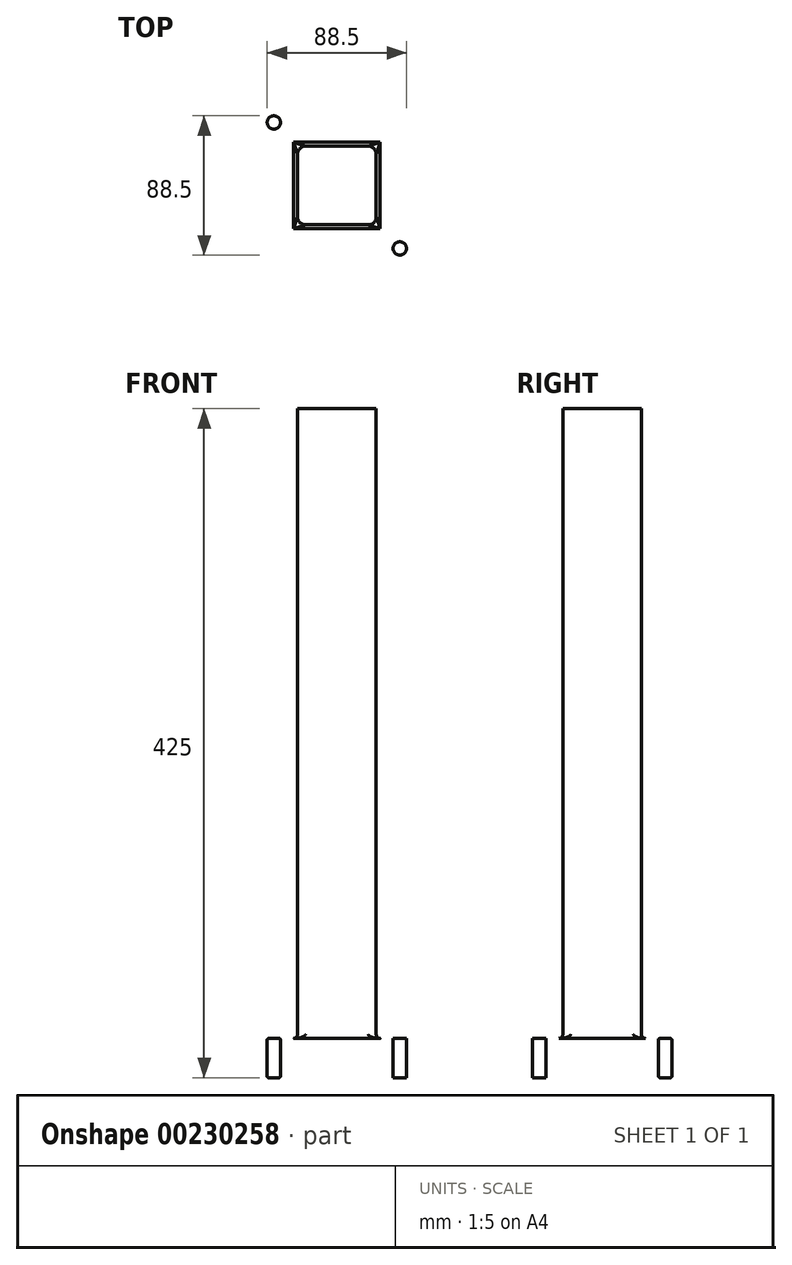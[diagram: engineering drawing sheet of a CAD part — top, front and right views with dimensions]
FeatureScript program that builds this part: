
annotation { "Feature Type Name" : "Feature", "Feature Type Description" : "" }
export const myFeature = defineFeature(function(context is Context, id is Id, definition is map)
    precondition{}
    {
        {
            var Q0;
            Q0=qCreatedBy(makeId("Front.planeOp"),FACE);
            var sketch = newSketch(context, id + "F0", { "sketchPlane" : qUnion([Q0])});
            skLineSegment(sketch, "E0.bottom", {"start": v(25, 200) * mm, "end": v(-25, 200) * mm});
            skLineSegment(sketch, "E0.top", {"start": v(25, -200) * mm, "end": v(-25, -200) * mm});
            skLineSegment(sketch, "E0.left", {"start": v(25, 200) * mm, "end": v(25, -200) * mm});
            skLineSegment(sketch, "E0.right", {"start": v(-25, 200) * mm, "end": v(-25, -200) * mm});
            skPoint(sketch, "E0.middle", {"position": v(0, 0) * mm});
            skLineSegment(sketch, "E1.bottom", {"start": v(-50, -200) * mm, "end": v(50, -200) * mm});
            skLineSegment(sketch, "E1.top", {"start": v(-50, -225) * mm, "end": v(50, -225) * mm});
            skLineSegment(sketch, "E1.left", {"start": v(-50, -200) * mm, "end": v(-50, -225) * mm});
            skLineSegment(sketch, "E1.right", {"start": v(50, -200) * mm, "end": v(50, -225) * mm});
            skSolve(sketch);
        }
        {
            var Q0;
            Q0=makeQuery(id+"F0.imprint","IMPRINT",FACE,{"disambiguationData":[TD([[makeQuery(id+"F0.imprint","IMPRINT",EDGE,{"derivedFrom":sQuery(id+"F0.wireOp",EDGE,"E1.top")}),1.0]])]});
            extrude(context, id + "F1", {"entities" : qUnion([Q0]), "endBound" : BoundingType.SYMMETRIC, "depth" : 100 * mm});
        }
        {
            var Q0;
            Q0=makeQuery(id+"F0.imprint","IMPRINT",FACE,{"disambiguationData":[TD([[makeQuery(id+"F0.imprint","IMPRINT",EDGE,{"derivedFrom":sQuery(id+"F0.wireOp",EDGE,"E0.bottom")}),1.0]])]});
            extrude(context, id + "F2", {"entities" : qUnion([Q0]), "operationType" : NewBodyOperationType.ADD, "endBound" : BoundingType.SYMMETRIC, "depth" : 50 * mm});
        }
        {
            var Q0;
            Q0=makeQuery(id+"F1.opExtrude","SWEPT_FACE",FACE,{"disambiguationData":[OSD([sQuery(id+"F0.wireOp",EDGE,"E1.bottom")])]});
            fillet(context, id + "F3", {"entities" : qUnion([Q0]), "radius" : 2.5 * mm, "tangentPropagation" : true, "allowEdgeOverflow" : false});
        }
        {
            var Q0;
            Q0=makeQuery(id+"F2.opExtrude","CAP_EDGE",EDGE,{"disambiguationData":[OSD([sQuery(id+"F0.wireOp",EDGE,"E0.right")])],"isStart":false});
            var Q1;
            Q1=makeQuery(id+"F2.opExtrude","CAP_EDGE",EDGE,{"disambiguationData":[OSD([sQuery(id+"F0.wireOp",EDGE,"E0.left")])],"isStart":false});
            var Q2;
            Q2=makeQuery(id+"F2.opExtrude","CAP_EDGE",EDGE,{"disambiguationData":[OSD([sQuery(id+"F0.wireOp",EDGE,"E0.right")])],"isStart":true});
            var Q3;
            Q3=makeQuery(id+"F2.opExtrude","CAP_EDGE",EDGE,{"disambiguationData":[OSD([sQuery(id+"F0.wireOp",EDGE,"E0.left")])],"isStart":true});
            fillet(context, id + "F4", {"entities" : qUnion([Q0, Q1, Q2, Q3]), "radius" : 5 * mm, "tangentPropagation" : true, "allowEdgeOverflow" : false});
        }
        {
            var Q0;
            Q0=makeQuery(id+"F1.opExtrude","SWEPT_FACE",FACE,{"disambiguationData":[OSD([sQuery(id+"F0.wireOp",EDGE,"E1.top")])]});
            var sketch = newSketch(context, id + "F5", { "sketchPlane" : qUnion([Q0])});
            skCircle(sketch, "E2", {"center": v(-40, 40) * mm, "radius": 4.25 * mm});
            skCircle(sketch, "E3.MirrorC", {"center": v(40, 40) * mm, "radius": 4.25 * mm});
            skCircle(sketch, "E4.MirrorC", {"center": v(-40, -40) * mm, "radius": 4.25 * mm});
            skCircle(sketch, "E5.MirrorC", {"center": v(40, -40) * mm, "radius": 4.25 * mm});
            skSolve(sketch);
        }
        {
            var Q0;
            Q0=makeQuery(id+"F5.imprint","IMPRINT",FACE,{"disambiguationData":[TD([[makeQuery(id+"F5.imprint","IMPRINT",EDGE,{"derivedFrom":sQuery(id+"F5.wireOp",EDGE,"E2")}),1.0]])]});
            var Q1;
            Q1=makeQuery(id+"F5.imprint","IMPRINT",FACE,{"disambiguationData":[TD([[makeQuery(id+"F5.imprint","IMPRINT",EDGE,{"derivedFrom":sQuery(id+"F5.wireOp",EDGE,"E3.MirrorC")}),-1.0]])]});
            var Q2;
            Q2=makeQuery(id+"F5.imprint","IMPRINT",FACE,{"disambiguationData":[TD([[makeQuery(id+"F5.imprint","IMPRINT",EDGE,{"derivedFrom":sQuery(id+"F5.wireOp",EDGE,"E5.MirrorC")}),1.0]])]});
            var Q3;
            Q3=makeQuery(id+"F5.imprint","IMPRINT",FACE,{"disambiguationData":[TD([[makeQuery(id+"F5.imprint","IMPRINT",EDGE,{"derivedFrom":sQuery(id+"F5.wireOp",EDGE,"E4.MirrorC")}),-1.0]])]});
            extrude(context, id + "F6", {"entities" : qUnion([Q0, Q1, Q2, Q3]), "operationType" : NewBodyOperationType.REMOVE, "oppositeDirection" : true, "depth" : 25 * mm});
        }
        {
            var Q0;
            Q0=makeQuery(id+"F6.boolean.opBoolean","COPY",EDGE,{"derivedFrom":makeQuery(id+"F6.opExtrude","CAP_EDGE",EDGE,{"disambiguationData":[OSD([sQuery(id+"F5.wireOp",EDGE,"E2")])],"isStart":true})});
            var Q1;
            Q1=makeQuery(id+"F6.boolean.opBoolean","COPY",EDGE,{"derivedFrom":makeQuery(id+"F6.opExtrude","CAP_EDGE",EDGE,{"disambiguationData":[OSD([sQuery(id+"F5.wireOp",EDGE,"E3.MirrorC")])],"isStart":true})});
            var Q2;
            Q2=makeQuery(id+"F6.boolean.opBoolean","COPY",EDGE,{"derivedFrom":makeQuery(id+"F6.opExtrude","CAP_EDGE",EDGE,{"disambiguationData":[OSD([sQuery(id+"F5.wireOp",EDGE,"E5.MirrorC")])],"isStart":true})});
            var Q3;
            Q3=makeQuery(id+"F6.boolean.opBoolean","COPY",EDGE,{"derivedFrom":makeQuery(id+"F6.opExtrude","CAP_EDGE",EDGE,{"disambiguationData":[OSD([sQuery(id+"F5.wireOp",EDGE,"E4.MirrorC")])],"isStart":true})});
            var Q4;
            Q4=makeQuery(id+"F6.boolean.opBoolean","COPY",EDGE,{"derivedFrom":makeQuery(id+"F6.opExtrude","CAP_EDGE",EDGE,{"disambiguationData":[OSD([sQuery(id+"F5.wireOp",EDGE,"E3.MirrorC")])],"isStart":false})});
            var Q5;
            Q5=makeQuery(id+"F6.boolean.opBoolean","COPY",EDGE,{"derivedFrom":makeQuery(id+"F6.opExtrude","CAP_EDGE",EDGE,{"disambiguationData":[OSD([sQuery(id+"F5.wireOp",EDGE,"E5.MirrorC")])],"isStart":false})});
            var Q6;
            Q6=makeQuery(id+"F6.boolean.opBoolean","COPY",EDGE,{"derivedFrom":makeQuery(id+"F6.opExtrude","CAP_EDGE",EDGE,{"disambiguationData":[OSD([sQuery(id+"F5.wireOp",EDGE,"E4.MirrorC")])],"isStart":false})});
            var Q7;
            Q7=makeQuery(id+"F6.boolean.opBoolean","COPY",EDGE,{"derivedFrom":makeQuery(id+"F6.opExtrude","CAP_EDGE",EDGE,{"disambiguationData":[OSD([sQuery(id+"F5.wireOp",EDGE,"E2")])],"isStart":false})});
            fillet(context, id + "F7", {"entities" : qUnion([Q0, Q1, Q2, Q3, Q4, Q5, Q6, Q7]), "radius" : 1 * mm, "tangentPropagation" : true, "allowEdgeOverflow" : false});
        }
    });
